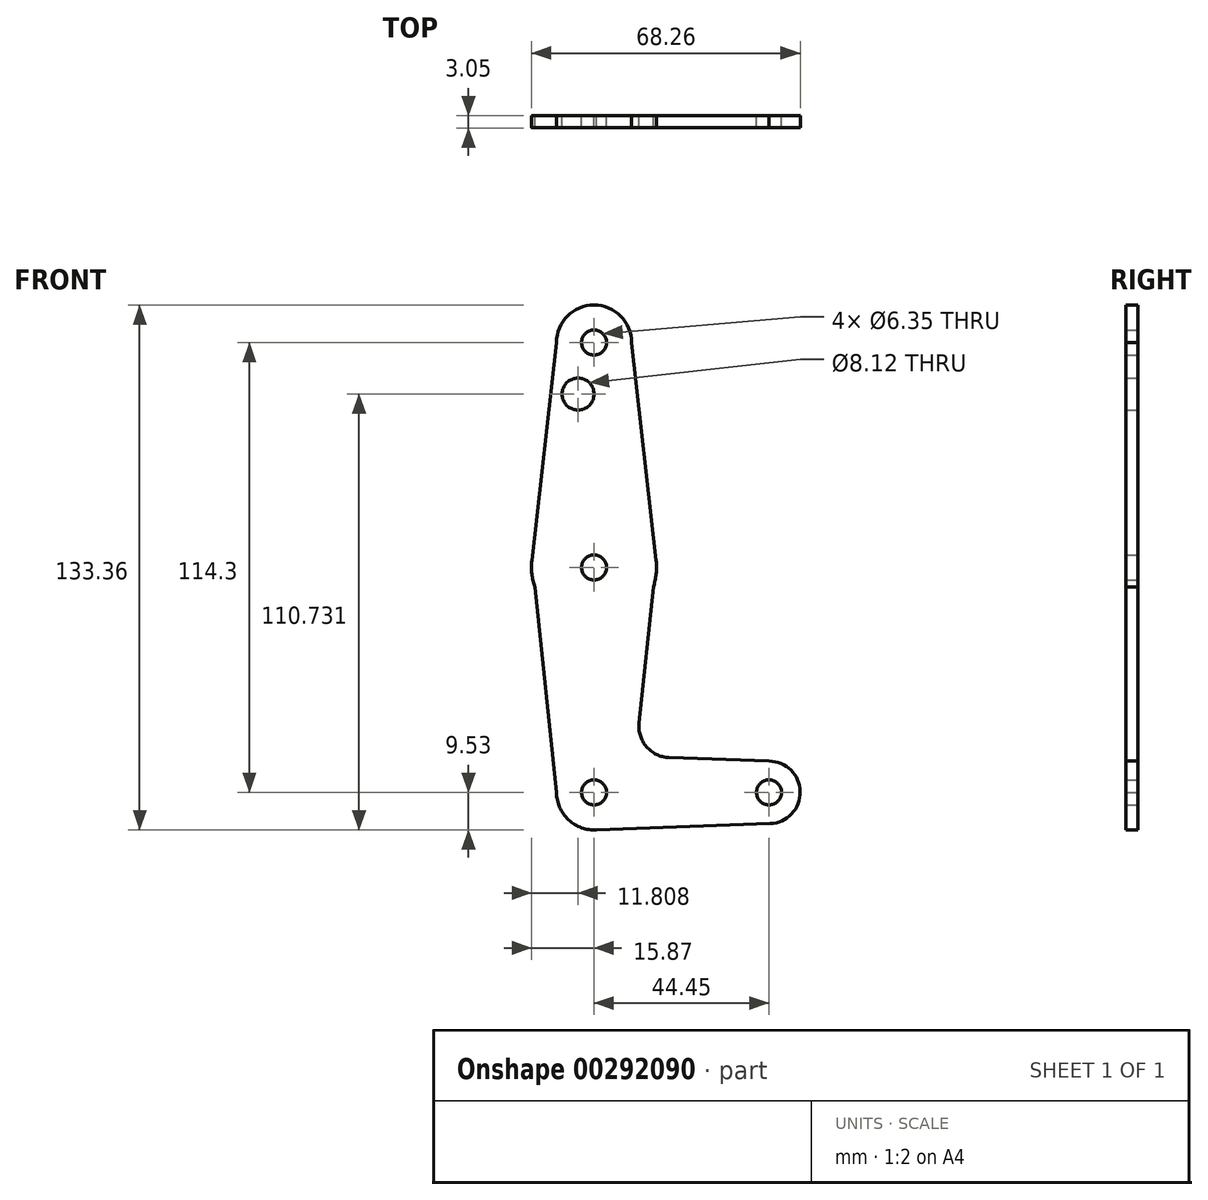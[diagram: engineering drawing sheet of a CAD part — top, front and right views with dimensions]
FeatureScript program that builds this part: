
annotation { "Feature Type Name" : "Feature", "Feature Type Description" : "" }
export const myFeature = defineFeature(function(context is Context, id is Id, definition is map)
    precondition{}
    {
        {
            var Q0;
            Q0=qCreatedBy(makeId("Front.planeOp"),FACE);
            var sketch = newSketch(context, id + "F0", { "sketchPlane" : qUnion([Q0])});
            skLineSegment(sketch, "E0", {"start": v(0, 0) * mm, "end": v(0, 114.3) * mm});
            skLineSegment(sketch, "E1", {"start": v(0, 0) * mm, "end": v(44.45, 0) * mm});
            skCircle(sketch, "E2", {"center": v(0, 114.3) * mm, "radius": 9.53 * mm});
            skCircle(sketch, "E3", {"center": v(0, 57.15) * mm, "radius": 15.88 * mm});
            skCircle(sketch, "E4", {"center": v(0, 0) * mm, "radius": 9.53 * mm});
            skCircle(sketch, "E5", {"center": v(44.45, 0) * mm, "radius": 7.94 * mm});
            skLineSegment(sketch, "E6", {"start": v(-9.53, 114.3) * mm, "end": v(-15.77, 58.93) * mm});
            skLineSegment(sketch, "E7", {"start": v(9.52, 114.3) * mm, "end": v(15.77, 58.93) * mm});
            skLineSegment(sketch, "E8", {"start": v(0, -9.53) * mm, "end": v(44.73, -7.93) * mm});
            skLineSegment(sketch, "E9", {"start": v(15.77, 58.93) * mm, "end": v(11.43, 17.62) * mm});
            skLineSegment(sketch, "E10", {"start": v(44.45, 7.94) * mm, "end": v(19.05, 8.85) * mm});
            skPoint(sketch, "E11.newPointA", {"position": v(0, 9.53) * mm});
            skArc(sketch, "E11.filletArc", {"start": v(11.43, 17.62) * mm, "mid": v(13.33, 11.58) * mm, "end": v(19.05, 8.85) * mm});
            skCircle(sketch, "E12", {"center": v(0, 114.3) * mm, "radius": 3.18 * mm});
            skCircle(sketch, "E13", {"center": v(0, 57.15) * mm, "radius": 3.18 * mm});
            skCircle(sketch, "E14", {"center": v(0, 0) * mm, "radius": 3.18 * mm});
            skCircle(sketch, "E15", {"center": v(44.45, 0) * mm, "radius": 3.18 * mm});
            skCircle(sketch, "E16", {"center": v(-4.06, 101.2) * mm, "radius": 4.06 * mm});
            skLineSegment(sketch, "E17", {"start": v(-15.77, 58.93) * mm, "end": v(-9.53, 0) * mm});
            skSolve(sketch);
        }
        {
            var Q0;
            Q0 = qSketchRegion(id + "F0", true);
            var Q1;
            {var subQ0=sQuery(id+"F0.wireOp",EDGE,"E14");var subQ1=sQuery(id+"F0.wireOp",EDGE,"E0");var subQ2=makeQuery(id+"F0.imprint","INTERSECT",VERTEX,{"derivedFrom":[subQ1,subQ0]});Q1=makeQuery(id+"F0.imprint","IMPRINT",FACE,{"disambiguationData":[TD([[makeQuery(id+"F0.imprint","IMPRINT",EDGE,{"disambiguationData":[TD([[subQ2,-1.0]])],"derivedFrom":subQ1}),-1.0]])]});}
            extrude(context, id + "F1", {"entities" : qUnion([Q0, Q1]), "depth" : 3.05 * mm});
        }
    });
